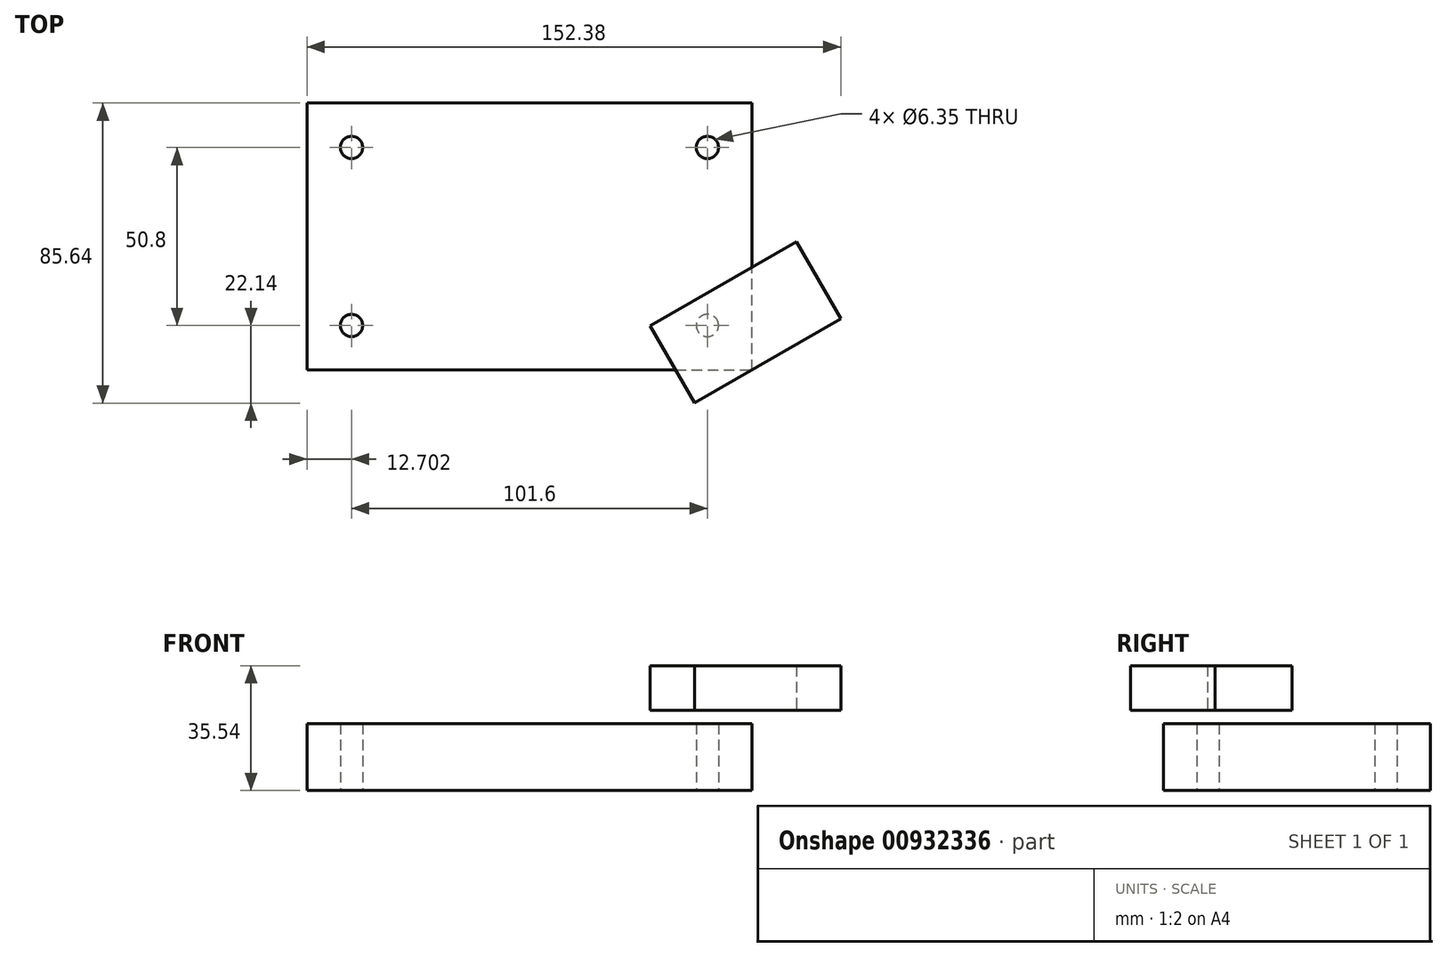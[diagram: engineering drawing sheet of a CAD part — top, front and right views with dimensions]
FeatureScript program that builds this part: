
annotation { "Feature Type Name" : "Feature", "Feature Type Description" : "" }
export const myFeature = defineFeature(function(context is Context, id is Id, definition is map)
    precondition{}
    {
        {
            var Q0;
            Q0=qCreatedBy(makeId("Top.planeOp"),FACE);
            var sketch = newSketch(context, id + "F0", { "sketchPlane" : qUnion([Q0])});
            skLineSegment(sketch, "E0.bottom", {"start": v(-87.7, 0) * mm, "end": v(39.3, 0) * mm});
            skLineSegment(sketch, "E0.top", {"start": v(-87.7, 76.2) * mm, "end": v(39.3, 76.2) * mm});
            skLineSegment(sketch, "E0.left", {"start": v(-87.7, 0) * mm, "end": v(-87.7, 76.2) * mm});
            skLineSegment(sketch, "E0.right", {"start": v(39.3, 0) * mm, "end": v(39.3, 76.2) * mm});
            skCircle(sketch, "E1", {"center": v(-75, 63.5) * mm, "radius": 3.18 * mm});
            skCircle(sketch, "E2.MirrorC", {"center": v(-75, 12.7) * mm, "radius": 3.18 * mm});
            skCircle(sketch, "E3.MirrorC", {"center": v(26.6, 63.5) * mm, "radius": 3.18 * mm});
            skCircle(sketch, "E4.MirrorC", {"center": v(26.6, 12.7) * mm, "radius": 3.18 * mm});
            skSolve(sketch);
        }
        {
            var Q0;
            Q0 = qSketchRegion(id + "F0", true);
            extrude(context, id + "F1", {"entities" : qUnion([Q0]), "depth" : 19.05 * mm, "offsetDistance" : 25.4 * mm});
        }
        {
            var Q0;
            Q0=makeQuery(id+"F1.opExtrude","SWEPT_FACE",FACE,{"disambiguationData":[OSD([sQuery(id+"F0.wireOp",EDGE,"E0.bottom")])]});
            var Q1;
            Q1=makeQuery(id+"F1.opExtrude","SWEPT_EDGE",EDGE,{"disambiguationData":[OSD([sQuery(id+"F0.wireOp",EDGE,"E0.bottom"),sQuery(id+"F0.wireOp",EDGE,"E0.right")])]});
            cPlane(context, id + "F2", {"entities" : qUnion([Q0, Q1]), "cplaneType" : CPlaneType.LINE_ANGLE, "offset" : 25.4 * mm, "angle" : 30 * degree, "oppositeDirection" : true, "width" : 152.4 * mm, "height" : 152.4 * mm});
        }
        {
            var Q0;
            Q0=qCreatedBy(id+"F2.planeOp",FACE);
            var sketch = newSketch(context, id + "F3", { "sketchPlane" : qUnion([Q0])});
            skLineSegment(sketch, "E5.bottom", {"start": v(-15.15, 35.54) * mm, "end": v(-63.34, 35.54) * mm});
            skLineSegment(sketch, "E5.top", {"start": v(-15.15, 22.82) * mm, "end": v(-63.34, 22.82) * mm});
            skLineSegment(sketch, "E5.left", {"start": v(-15.15, 35.54) * mm, "end": v(-15.15, 22.82) * mm});
            skLineSegment(sketch, "E5.right", {"start": v(-63.34, 35.54) * mm, "end": v(-63.34, 22.82) * mm});
            skSolve(sketch);
        }
        {
            var Q0;
            Q0 = qSketchRegion(id + "F3", true);
            extrude(context, id + "F4", {"entities" : qUnion([Q0]), "depth" : 25.4 * mm, "offsetDistance" : 25.4 * mm});
        }
    });
